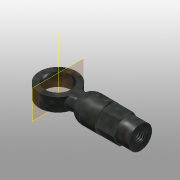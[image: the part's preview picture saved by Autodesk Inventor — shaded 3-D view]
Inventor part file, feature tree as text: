
AUTODESK INVENTOR PART (.ipt)
format: ipt  version: 2016 (Build 200138000, 138)  size: 242,176 bytes
history: native  units: mm
features: sketch x11, extrude x6, revolve x4, projected_geometry x4, hole x2, plane x1, other x1
ambient origin geometry x8: Origin, YZ Plane, XZ Plane, XY Plane, X Axis, Y Axis, Z Axis, Center Point
bodies: Solid1 (feature_tree)
feature tree (29):
  revolve  "Revolution1"  [1 undecoded]
  extrude  "Extrusion1"  Depth=10.2mm
  plane  "Work Plane1"
  revolve  "Revolution2"  [1 undecoded]
  hole  "Hole2"  [1 undecoded]
  extrude  "Extrusion2"  TaperAngle=0.0deg  [1 undecoded]
  extrude  "Extrusion3"  TaperAngle=90.0deg  [1 undecoded]
  hole  "Hole3"  [1 undecoded]
  extrude  "Extrusion4"  Depth=5.0mm
  extrude  "Extrusion5"  Depth=10.0mm
  revolve  "Revolution3"  [1 undecoded]
  revolve  "Revolution4"  [1 undecoded]
  extrude  "Extrusion6"  TaperAngle=90.0deg  [1 undecoded]
  sketch  "Sketch1"  dims[d0=2.85mm d1=3.5mm]
  sketch  "Sketch2"  dims[d2=90.0deg d3=10.2mm]
  other  "Work Axis1"
  sketch  "Sketch3"  dims[d4=10.9mm d7=8.0mm]
  sketch  "Sketch4"  dims[d10=2.9mm d11=0.0mm d12=19.198622mm]
  sketch  "Sketch5"  dims[d13=19.198622mm d25=0.0mm]
  sketch  "Sketch6"  dims[d26=6.4mm d27=90.0deg]
  sketch  "Sketch9"  dims[d28=1.0mm d29=1.0mm d30=4.0mm d31=2.0mm d32=90.0deg d33=0.5mm d34=20.594885mm d35=5.0mm]
  sketch  "Sketch10"  dims[d36=4.0mm d37=0.0mm d38=5.0mm]
  sketch  "Sketch11"  dims[d39=3.0mm d40=0.0mm d41=10.0mm d42=10.0mm]
  sketch  "Sketch12"  dims[d43=2.013mm d44=4.0mm d45=4.0mm d46=2.0mm d47=90.0deg d48=5.7mm d49=20.594885mm d50=8.0mm]
  sketch  "Sketch13"  dims[d51=0.0mm d52=0.0mm d53=10.0mm d54=0.0mm d55=90.0deg d56=90.0deg d57=10.0mm d58=0.0mm]
  projected_geometry  "Projected Loop1"
  projected_geometry  "Project Cut Edges1"
  projected_geometry  "Project Cut Edges2"
  projected_geometry  "Project Cut Edges3"
note: 9 required parameter values undecoded (feature->parameter linkage not recoverable at this tier; creation-order binding heuristic only, values carry confidence <= 0.55)